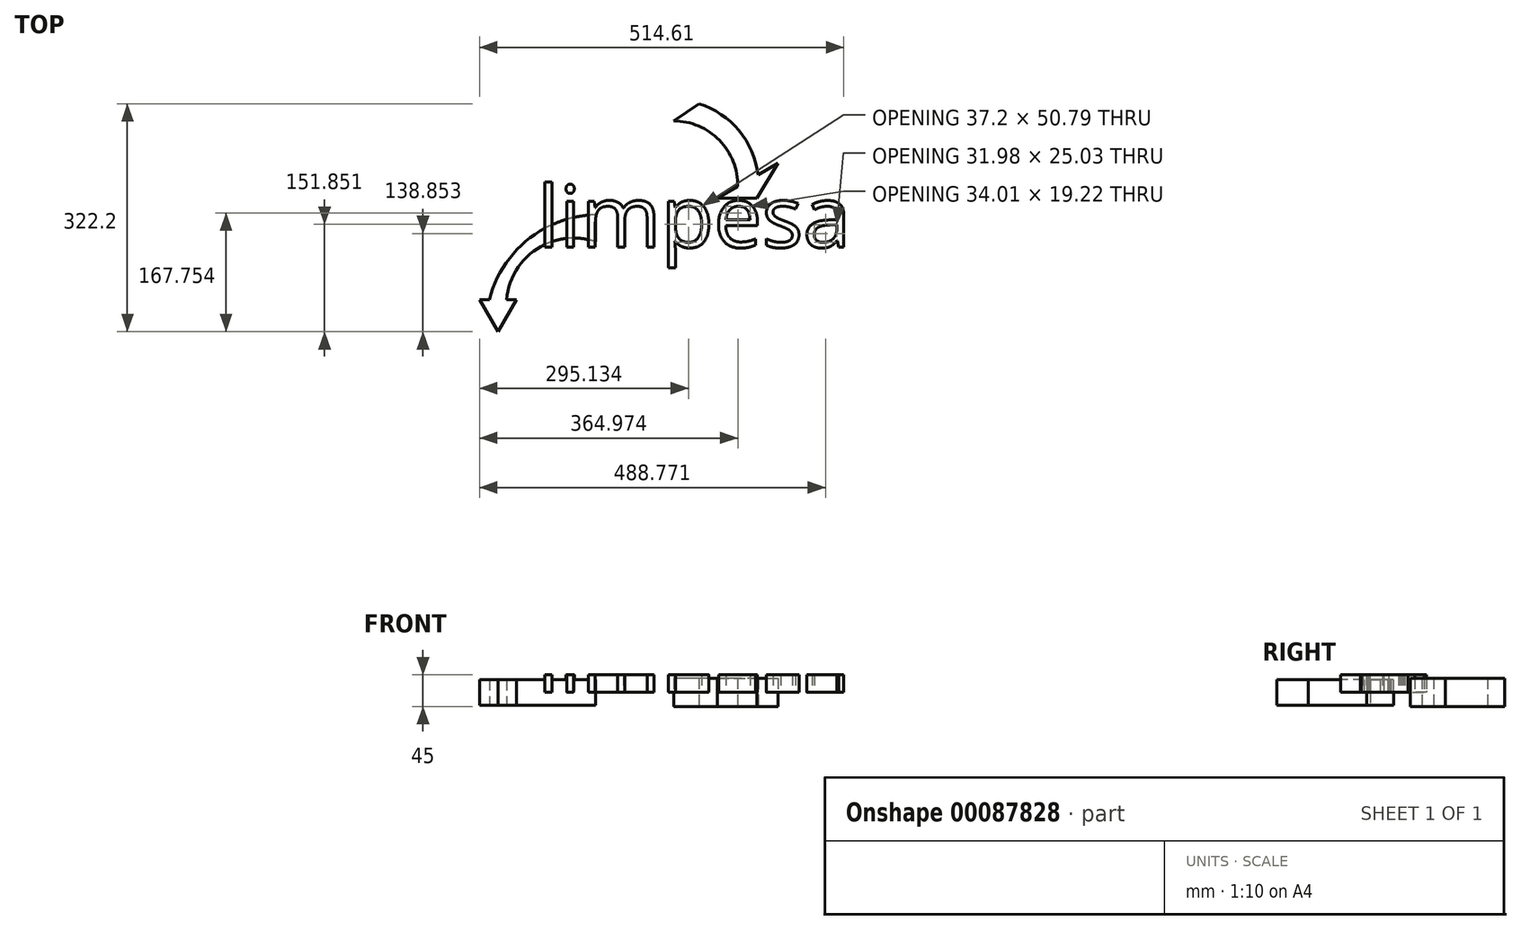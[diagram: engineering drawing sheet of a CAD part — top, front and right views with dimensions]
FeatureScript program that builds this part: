
annotation { "Feature Type Name" : "Feature", "Feature Type Description" : "" }
export const myFeature = defineFeature(function(context is Context, id is Id, definition is map)
    precondition{}
    {
        {
            var Q0;
            Q0=qCreatedBy(makeId("Top.planeOp"),FACE);
            var sketch = newSketch(context, id + "F0", { "sketchPlane" : qUnion([Q0])});
            skLineSegment(sketch, "E0", {"start": v(62.13, 141.41) * mm, "end": v(117.94, 141.41) * mm});
            skLineSegment(sketch, "E1", {"start": v(117.94, 141.41) * mm, "end": v(147.35, 190.76) * mm});
            skLineSegment(sketch, "E2", {"start": v(105.62, 168.77) * mm, "end": v(117.94, 141.41) * mm, "construction": true});
            skLineSegment(sketch, "E3", {"start": v(84.32, 153.36) * mm, "end": v(90.58, 157.9) * mm, "construction": true});
            skLineSegment(sketch, "E4", {"start": v(62.13, 141.41) * mm, "end": v(147.35, 190.76) * mm});
            skLineSegment(sketch, "E5", {"start": v(35.99, 274.84) * mm, "end": v(0, 250.6) * mm});
            skArc(sketch, "E6", {"start": v(90.58, 157.9) * mm, "mid": v(64.81, 223.32) * mm, "end": v(0, 250.6) * mm});
            skArc(sketch, "E7.0", {"start": v(119.46, 174.61) * mm, "mid": v(92.48, 237.02) * mm, "end": v(35.99, 274.84) * mm});
            skSolve(sketch);
        }
        {
            var Q0;
            Q0=qSketchRegion(id+"F0",true);
            extrude(context, id + "F1", {"entities" : qUnion([Q0]), "endBound" : BoundingType.SYMMETRIC, "depth" : 40 * mm});
        }
        {
            var Q0;
            Q0=qCreatedBy(makeId("Top.planeOp"),FACE);
            var sketch = newSketch(context, id + "F2", { "sketchPlane" : qUnion([Q0])});
            skCircle(sketch, "E8.cCircle", {"center": v(-248.03, -17.36) * mm, "radius": 15 * mm, "construction": true});
            skLineSegment(sketch, "E8.0", {"start": v(-274, -2.36) * mm, "end": v(-222.05, -2.36) * mm});
            skLineSegment(sketch, "E8.1", {"start": v(-222.05, -2.36) * mm, "end": v(-248.03, -47.36) * mm});
            skLineSegment(sketch, "E8.2", {"start": v(-248.03, -47.36) * mm, "end": v(-274, -2.36) * mm});
            skPoint(sketch, "E8.0.midPoint", {"position": v(-248.03, -2.36) * mm});
            skLineSegment(sketch, "E9", {"start": v(-110.42, 117.93) * mm, "end": v(-110.42, 79.86) * mm});
            skArc(sketch, "E10", {"start": v(-110.42, 79.86) * mm, "mid": v(-193.4, 69.58) * mm, "end": v(-236.04, -2.36) * mm});
            skArc(sketch, "E11", {"start": v(-110.42, 117.93) * mm, "mid": v(-205.65, 83.1) * mm, "end": v(-260.25, -2.36) * mm});
            skSolve(sketch);
        }
        {
            var Q0;
            Q0=qSketchRegion(id+"F2",true);
            extrude(context, id + "F3", {"entities" : qUnion([Q0]), "endBound" : BoundingType.SYMMETRIC, "depth" : 35.64 * mm});
        }
        {
            var Q0;
            Q0=qCreatedBy(makeId("Top.planeOp"),FACE);
            var sketch = newSketch(context, id + "F4", { "sketchPlane" : qUnion([Q0])});
            skText(sketch, "E12", { "text": "limpesa\n", "fontName": "OpenSans-Regular.ttf"});
            const initialGuessF4  = {"E12": [-0.1923, 0.07203, 1, 0, 0.0875]};
            skSetInitialGuess(sketch, initialGuessF4);
            skSolve(sketch);
        }
        {
            var Q0;
            Q0=qSketchRegion(id+"F4",true);
            extrude(context, id + "F5", {"entities" : qUnion([Q0]), "operationType" : NewBodyOperationType.ADD, "depth" : 25 * mm});
        }
    });
